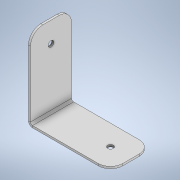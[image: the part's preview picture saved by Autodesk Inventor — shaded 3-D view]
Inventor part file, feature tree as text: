
AUTODESK INVENTOR PART (.ipt)
format: ipt  version: 2021 (Build 250183000, 183)  size: 142,848 bytes
history: native  units: mm
features: sheet_metal_op x4, sketch x4, chamfer x2, hole x2, other x2
ambient origin geometry x8: Origin, YZ Plane, XZ Plane, XY Plane, X Axis, Y Axis, Z Axis, Center Point
bodies: Solid1 (feature_tree)
feature tree (14):
  sheet_metal_op  "Face1"
  chamfer  "Corner Round1"
  hole  "Hole2"  [1 undecoded]
  sheet_metal_op  "Flange1"
  chamfer  "Corner Round2"
  hole  "Hole3"  [1 undecoded]
  sketch  "Sketch1"  dims[d0=20.0mm d1=10.0mm]
  other  "Plate1"
  sketch  "Sketch3"  dims[d4=0.5mm d5=3.0mm]
  sketch  "Sketch4"  dims[d15=1.4mm d16=6.0mm d17=4.0mm d18=2.0mm d19=90.0deg d20=0.5mm]
  other  "Plate2"
  sheet_metal_op  "Bend1"
  sheet_metal_op  "Corner1"
  sketch  "Sketch5"  dims[d21=0.0mm d22=5.0mm d23=5.0mm d24=0.5mm d25=0.25mm d26=1.0mm d27=0.5mm d28=20.0mm d29=90.0deg d30=0.5mm d31=2.0mm d32=0.5mm d33=0.5mm d34=3.0mm d35=1.4mm d36=6.0mm d37=4.0mm d38=2.0mm d39=90.0deg d40=0.5mm d41=0.0mm d42=5.0mm d43=5.0mm]
note: 2 required parameter values undecoded (feature->parameter linkage not recoverable at this tier; creation-order binding heuristic only, values carry confidence <= 0.55)
